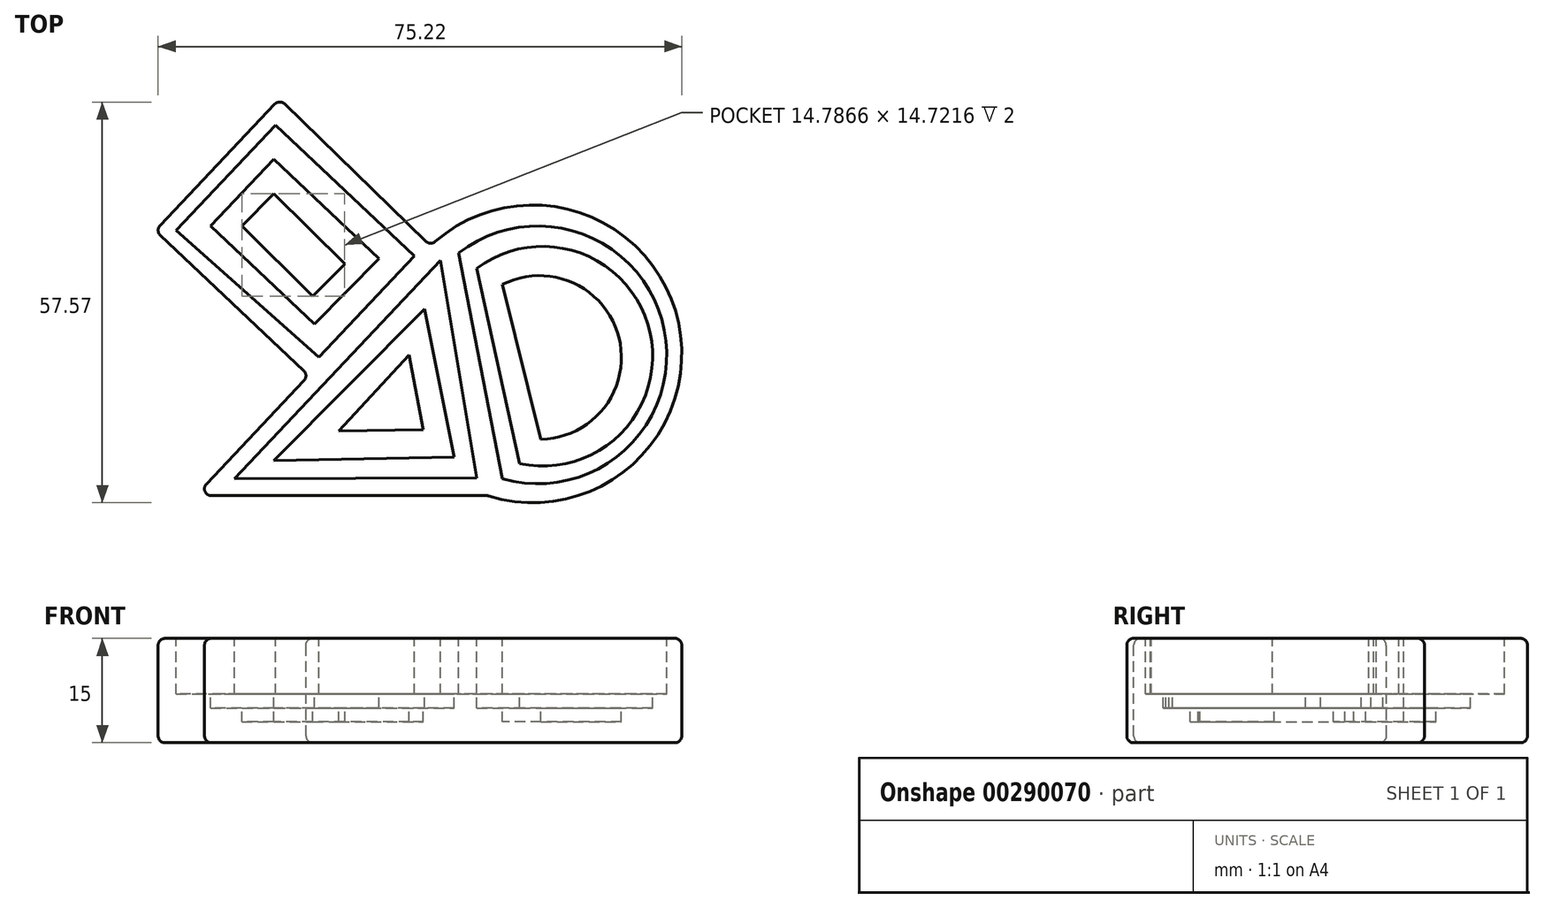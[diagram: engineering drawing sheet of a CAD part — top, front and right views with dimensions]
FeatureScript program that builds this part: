
annotation { "Feature Type Name" : "Feature", "Feature Type Description" : "" }
export const myFeature = defineFeature(function(context is Context, id is Id, definition is map)
    precondition{}
    {
        {
            var Q0;
            Q0=qCreatedBy(makeId("Top.planeOp"),FACE);
            var sketch = newSketch(context, id + "F0", { "sketchPlane" : qUnion([Q0])});
            skLineSegment(sketch, "E0", {"start": v(-46.18, 20.15) * mm, "end": v(-28.32, 39.05) * mm});
            skLineSegment(sketch, "E1", {"start": v(-28.32, 39.05) * mm, "end": v(-6.65, 17.95) * mm});
            skArc(sketch, "E2", {"start": v(1.58, -17.95) * mm, "mid": v(28.9, 7.21) * mm, "end": v(-6.65, 17.95) * mm});
            skLineSegment(sketch, "E3", {"start": v(-46.18, 20.15) * mm, "end": v(-24.13, -0.7) * mm});
            skLineSegment(sketch, "E4", {"start": v(-24.13, -0.7) * mm, "end": v(-40.43, -17.95) * mm});
            skLineSegment(sketch, "E5", {"start": v(-40.43, -17.95) * mm, "end": v(1.58, -17.95) * mm});
            skSolve(sketch);
        }
        {
            var Q0;
            Q0=makeQuery(id+"F0.imprint","IMPRINT",FACE,{"disambiguationData":[TD([[makeQuery(id+"F0.imprint","IMPRINT",EDGE,{"derivedFrom":sQuery(id+"F0.wireOp",EDGE,"E0")}),-1.0]])]});
            extrude(context, id + "F1", {"entities" : qUnion([Q0]), "depth" : 15 * mm});
        }
        {
            var Q0;
            Q0=makeQuery(id+"F1.opExtrude","CAP_FACE",FACE,{"disambiguationData":[OSD([sQuery(id+"F0.wireOp",EDGE,"E0"),sQuery(id+"F0.wireOp",EDGE,"E1"),sQuery(id+"F0.wireOp",EDGE,"E2"),sQuery(id+"F0.wireOp",EDGE,"E3"),sQuery(id+"F0.wireOp",EDGE,"45Map7S6-xY7Q-KK4a-DzPV-caNNbyCEZp7A"),sQuery(id+"F0.wireOp",EDGE,"oJqrQrKj-ZpfX-hNZr-h9x0-pQ9A5762xfXI"),sQuery(id+"F0.wireOp",EDGE,"E4"),sQuery(id+"F0.wireOp",EDGE,"E5")])],"isStart":false});
            var sketch = newSketch(context, id + "F2", { "sketchPlane" : qUnion([Q0])});
            skLineSegment(sketch, "E6", {"start": v(-34.83, -15.53) * mm, "end": v(-5.2, 15.83) * mm});
            skLineSegment(sketch, "E7", {"start": v(-5.2, 15.83) * mm, "end": v(0, -15.41) * mm});
            skLineSegment(sketch, "E8", {"start": v(0, -15.41) * mm, "end": v(-34.83, -15.53) * mm});
            skLineSegment(sketch, "E9", {"start": v(-43.18, 20.15) * mm, "end": v(-28.87, 35.28) * mm});
            skLineSegment(sketch, "E10", {"start": v(-28.87, 35.28) * mm, "end": v(-8.98, 16.5) * mm});
            skLineSegment(sketch, "E11", {"start": v(-8.98, 16.5) * mm, "end": v(-22.7, 1.97) * mm});
            skLineSegment(sketch, "E12", {"start": v(-22.7, 1.97) * mm, "end": v(-43.18, 20.15) * mm});
            skArc(sketch, "E13", {"start": v(3.7, -15.54) * mm, "mid": v(26.95, 5.82) * mm, "end": v(-2.6, 16.92) * mm});
            skPoint(sketch, "E13.endSnap0", {"position": v(-2.6, 0.2) * mm});
            skLineSegment(sketch, "E14", {"start": v(-2.6, 16.92) * mm, "end": v(3.7, -15.54) * mm});
            skSolve(sketch);
        }
        {
            var Q0;
            Q0=makeQuery(id+"F2.imprint","IMPRINT",FACE,{"disambiguationData":[TD([[makeQuery(id+"F2.imprint","IMPRINT",EDGE,{"derivedFrom":sQuery(id+"F2.wireOp",EDGE,"E13")}),1.0]])]});
            var Q1;
            Q1=makeQuery(id+"F2.imprint","IMPRINT",FACE,{"disambiguationData":[TD([[makeQuery(id+"F2.imprint","IMPRINT",EDGE,{"derivedFrom":sQuery(id+"F2.wireOp",EDGE,"E6")}),-1.0]])]});
            var Q2;
            Q2=makeQuery(id+"F2.imprint","IMPRINT",FACE,{"disambiguationData":[TD([[makeQuery(id+"F2.imprint","IMPRINT",EDGE,{"derivedFrom":sQuery(id+"F2.wireOp",EDGE,"E9")}),-1.0]])]});
            var Q3;
            Q3=makeQuery(id+"F2.imprint","IMPRINT",FACE,{"disambiguationData":[TD([[makeQuery(id+"F2.imprint","IMPRINT",EDGE,{"derivedFrom":sQuery(id+"F2.wireOp",EDGE,"E75luK8p-h0mA-NWcP-ZvuT-SGWaBSsSdRoQ")}),1.0]])]});
            extrude(context, id + "F3", {"entities" : qUnion([Q0, Q1, Q2, Q3]), "operationType" : NewBodyOperationType.REMOVE, "oppositeDirection" : true, "depth" : 8 * mm});
        }
        {
            var Q0;
            Q0=makeQuery(id+"F1.opExtrude","CAP_FACE",FACE,{"disambiguationData":[OSD([sQuery(id+"F0.wireOp",EDGE,"E0"),sQuery(id+"F0.wireOp",EDGE,"E1"),sQuery(id+"F0.wireOp",EDGE,"E2"),sQuery(id+"F0.wireOp",EDGE,"E3"),sQuery(id+"F0.wireOp",EDGE,"45Map7S6-xY7Q-KK4a-DzPV-caNNbyCEZp7A"),sQuery(id+"F0.wireOp",EDGE,"oJqrQrKj-ZpfX-hNZr-h9x0-pQ9A5762xfXI"),sQuery(id+"F0.wireOp",EDGE,"E4"),sQuery(id+"F0.wireOp",EDGE,"E5")])],"isStart":true});
            var Q1;
            Q1=makeQuery(id+"F3.boolean.opBoolean","COPY",EDGE,{"derivedFrom":makeQuery(id+"F3.opExtrude","CAP_EDGE",EDGE,{"disambiguationData":[OSD([sQuery(id+"F2.wireOp",EDGE,"E10")])],"isStart":true})});
            var Q2;
            Q2=makeQuery(id+"F3.boolean.opBoolean","COPY",EDGE,{"derivedFrom":makeQuery(id+"F3.opExtrude","CAP_EDGE",EDGE,{"disambiguationData":[OSD([sQuery(id+"F2.wireOp",EDGE,"E9")])],"isStart":true})});
            var Q3;
            Q3=makeQuery(id+"F3.boolean.opBoolean","COPY",EDGE,{"derivedFrom":makeQuery(id+"F3.opExtrude","CAP_EDGE",EDGE,{"disambiguationData":[OSD([sQuery(id+"F2.wireOp",EDGE,"E12")])],"isStart":true})});
            var Q4;
            Q4=makeQuery(id+"F3.boolean.opBoolean","COPY",EDGE,{"derivedFrom":makeQuery(id+"F3.opExtrude","CAP_EDGE",EDGE,{"disambiguationData":[OSD([sQuery(id+"F2.wireOp",EDGE,"E11")])],"isStart":true})});
            var Q5;
            Q5=makeQuery(id+"F3.boolean.opBoolean","COPY",EDGE,{"derivedFrom":makeQuery(id+"F3.opExtrude","CAP_EDGE",EDGE,{"disambiguationData":[OSD([sQuery(id+"F2.wireOp",EDGE,"E8")])],"isStart":true})});
            var Q6;
            Q6=makeQuery(id+"F3.boolean.opBoolean","COPY",EDGE,{"derivedFrom":makeQuery(id+"F3.opExtrude","CAP_EDGE",EDGE,{"disambiguationData":[OSD([sQuery(id+"F2.wireOp",EDGE,"E6")])],"isStart":true})});
            var Q7;
            Q7=makeQuery(id+"F3.boolean.opBoolean","COPY",EDGE,{"derivedFrom":makeQuery(id+"F3.opExtrude","CAP_EDGE",EDGE,{"disambiguationData":[OSD([sQuery(id+"F2.wireOp",EDGE,"E7")])],"isStart":true})});
            var Q8;
            Q8=makeQuery(id+"F3.boolean.opBoolean","COPY",EDGE,{"derivedFrom":makeQuery(id+"F3.opExtrude","CAP_EDGE",EDGE,{"disambiguationData":[OSD([sQuery(id+"F2.wireOp",EDGE,"E14")])],"isStart":true})});
            var Q9;
            Q9=makeQuery(id+"F3.boolean.opBoolean","COPY",EDGE,{"derivedFrom":makeQuery(id+"F3.opExtrude","CAP_EDGE",EDGE,{"disambiguationData":[OSD([sQuery(id+"F2.wireOp",EDGE,"E13")])],"isStart":true})});
            var Q10;
            Q10=makeQuery(id+"F3.boolean.opBoolean","COPY",EDGE,{"derivedFrom":makeQuery(id+"F3.opExtrude","CAP_EDGE",EDGE,{"disambiguationData":[OSD([sQuery(id+"F2.wireOp",EDGE,"RLaE2rvH-VrAM-fzAG-Qmya-pUEfVkDLwuKn")])],"isStart":true})});
            var Q11;
            Q11=makeQuery(id+"F3.boolean.opBoolean","COPY",EDGE,{"derivedFrom":makeQuery(id+"F3.opExtrude","CAP_EDGE",EDGE,{"disambiguationData":[OSD([sQuery(id+"F2.wireOp",EDGE,"jPx8ZiLx-Io0g-C835-jTOn-4QVJeUnpCxqh")])],"isStart":true})});
            var Q12;
            Q12=makeQuery(id+"F3.boolean.opBoolean","COPY",EDGE,{"derivedFrom":makeQuery(id+"F3.opExtrude","CAP_EDGE",EDGE,{"disambiguationData":[OSD([sQuery(id+"F2.wireOp",EDGE,"pincXrsu-reRM-YMyk-YWri-BdmM8ugr5dqy")])],"isStart":true})});
            var Q13;
            Q13=makeQuery(id+"F3.boolean.opBoolean","COPY",EDGE,{"derivedFrom":makeQuery(id+"F3.opExtrude","CAP_EDGE",EDGE,{"disambiguationData":[OSD([sQuery(id+"F2.wireOp",EDGE,"E75luK8p-h0mA-NWcP-ZvuT-SGWaBSsSdRoQ")])],"isStart":true})});
            var Q14;
            Q14=makeQuery(id+"F1.opExtrude","CAP_EDGE",EDGE,{"disambiguationData":[OSD([sQuery(id+"F0.wireOp",EDGE,"E2")])],"isStart":false});
            var Q15;
            Q15=makeQuery(id+"F1.opExtrude","CAP_EDGE",EDGE,{"disambiguationData":[OSD([sQuery(id+"F0.wireOp",EDGE,"oJqrQrKj-ZpfX-hNZr-h9x0-pQ9A5762xfXI")])],"isStart":false});
            var Q16;
            Q16=makeQuery(id+"F1.opExtrude","CAP_EDGE",EDGE,{"disambiguationData":[OSD([sQuery(id+"F0.wireOp",EDGE,"45Map7S6-xY7Q-KK4a-DzPV-caNNbyCEZp7A")])],"isStart":false});
            var Q17;
            Q17=makeQuery(id+"F1.opExtrude","CAP_EDGE",EDGE,{"disambiguationData":[OSD([sQuery(id+"F0.wireOp",EDGE,"E5")])],"isStart":false});
            var Q18;
            Q18=makeQuery(id+"F1.opExtrude","CAP_EDGE",EDGE,{"disambiguationData":[OSD([sQuery(id+"F0.wireOp",EDGE,"E4")])],"isStart":false});
            var Q19;
            Q19=makeQuery(id+"F1.opExtrude","CAP_EDGE",EDGE,{"disambiguationData":[OSD([sQuery(id+"F0.wireOp",EDGE,"E3")])],"isStart":false});
            var Q20;
            Q20=makeQuery(id+"F1.opExtrude","CAP_EDGE",EDGE,{"disambiguationData":[OSD([sQuery(id+"F0.wireOp",EDGE,"E0")])],"isStart":false});
            var Q21;
            Q21=makeQuery(id+"F1.opExtrude","CAP_EDGE",EDGE,{"disambiguationData":[OSD([sQuery(id+"F0.wireOp",EDGE,"E1")])],"isStart":false});
            var Q22;
            Q22=makeQuery(id+"F1.opExtrude","SWEPT_EDGE",EDGE,{"disambiguationData":[OSD([sQuery(id+"F0.wireOp",EDGE,"45Map7S6-xY7Q-KK4a-DzPV-caNNbyCEZp7A"),sQuery(id+"F0.wireOp",EDGE,"E5")])]});
            var Q23;
            Q23=makeQuery(id+"F1.opExtrude","SWEPT_FACE",FACE,{"disambiguationData":[OSD([sQuery(id+"F0.wireOp",EDGE,"oJqrQrKj-ZpfX-hNZr-h9x0-pQ9A5762xfXI")])]});
            var Q24;
            Q24=makeQuery(id+"F1.opExtrude","SWEPT_EDGE",EDGE,{"disambiguationData":[OSD([sQuery(id+"F0.wireOp",EDGE,"E1"),sQuery(id+"F0.wireOp",EDGE,"E2")])]});
            var Q25;
            Q25=makeQuery(id+"F1.opExtrude","SWEPT_FACE",FACE,{"disambiguationData":[OSD([sQuery(id+"F0.wireOp",EDGE,"E1")])]});
            var Q26;
            Q26=makeQuery(id+"F1.opExtrude","SWEPT_EDGE",EDGE,{"disambiguationData":[OSD([sQuery(id+"F0.wireOp",EDGE,"E0"),sQuery(id+"F0.wireOp",EDGE,"E1")])]});
            var Q27;
            Q27=makeQuery(id+"F1.opExtrude","SWEPT_EDGE",EDGE,{"disambiguationData":[OSD([sQuery(id+"F0.wireOp",EDGE,"E0"),sQuery(id+"F0.wireOp",EDGE,"E3")])]});
            var Q28;
            Q28=makeQuery(id+"F1.opExtrude","SWEPT_EDGE",EDGE,{"disambiguationData":[OSD([sQuery(id+"F0.wireOp",EDGE,"E4"),sQuery(id+"F0.wireOp",EDGE,"E5")])]});
            var Q29;
            Q29=makeQuery(id+"F1.opExtrude","SWEPT_EDGE",EDGE,{"disambiguationData":[OSD([sQuery(id+"F0.wireOp",EDGE,"E3"),sQuery(id+"F0.wireOp",EDGE,"E4")])]});
            var Q30;
            Q30=makeQuery(id+"F1.opExtrude","SWEPT_FACE",FACE,{"disambiguationData":[OSD([sQuery(id+"F0.wireOp",EDGE,"E5")])]});
            var Q31;
            Q31=makeQuery(id+"F1.opExtrude","SWEPT_EDGE",EDGE,{"disambiguationData":[OSD([sQuery(id+"F0.wireOp",EDGE,"E2"),sQuery(id+"F0.wireOp",EDGE,"oJqrQrKj-ZpfX-hNZr-h9x0-pQ9A5762xfXI")])]});
            fillet(context, id + "F4", {"entities" : qUnion([Q0, Q1, Q2, Q3, Q4, Q5, Q6, Q7, Q8, Q9, Q10, Q11, Q12, Q13, Q14, Q15, Q16, Q17, Q18, Q19, Q20, Q21, Q22, Q23, Q24, Q25, Q26, Q27, Q28, Q29, Q30, Q31]), "radius" : 1 * mm, "tangentPropagation" : true, "allowEdgeOverflow" : false});
        }
        {
            var Q0;
            Q0=makeQuery(id+"F3.boolean.opBoolean","COPY",FACE,{"derivedFrom":makeQuery(id+"F3.opExtrude","CAP_FACE",FACE,{"disambiguationData":[OSD([sQuery(id+"F2.wireOp",EDGE,"E9"),sQuery(id+"F2.wireOp",EDGE,"E10"),sQuery(id+"F2.wireOp",EDGE,"E11"),sQuery(id+"F2.wireOp",EDGE,"E12")])],"isStart":false})});
            var sketch = newSketch(context, id + "F5", { "sketchPlane" : qUnion([Q0])});
            skLineSegment(sketch, "E15", {"start": v(-3.25, -12.4) * mm, "end": v(-7.5, 8.88) * mm});
            skLineSegment(sketch, "E16", {"start": v(-7.5, 8.88) * mm, "end": v(-29.17, -12.9) * mm});
            skLineSegment(sketch, "E17", {"start": v(-29.17, -12.9) * mm, "end": v(-3.25, -12.4) * mm});
            skLineSegment(sketch, "E18", {"start": v(-14.05, 16.12) * mm, "end": v(-29.17, 30.4) * mm});
            skLineSegment(sketch, "E19", {"start": v(-29.17, 30.4) * mm, "end": v(-38.22, 20.83) * mm});
            skLineSegment(sketch, "E20", {"start": v(-38.22, 20.83) * mm, "end": v(-23.31, 6.74) * mm});
            skLineSegment(sketch, "E21", {"start": v(-23.31, 6.74) * mm, "end": v(-14.05, 16.12) * mm});
            skArc(sketch, "E22", {"start": v(6.18, -13.33) * mm, "mid": v(24.89, 5.49) * mm, "end": v(0, 14.7) * mm});
            skLineSegment(sketch, "E23", {"start": v(0, 14.7) * mm, "end": v(6.18, -13.33) * mm});
            skSolve(sketch);
        }
        {
            var Q0;
            Q0 = qSketchRegion(id + "F5", true);
            extrude(context, id + "F6", {"entities" : qUnion([Q0]), "operationType" : NewBodyOperationType.REMOVE, "oppositeDirection" : true, "depth" : 2 * mm});
        }
        {
            var Q0;
            Q0=makeQuery(id+"F6.boolean.opBoolean","COPY",FACE,{"derivedFrom":makeQuery(id+"F6.opExtrude","CAP_FACE",FACE,{"disambiguationData":[OSD([sQuery(id+"F5.wireOp",EDGE,"E22"),sQuery(id+"F5.wireOp",EDGE,"E23")])],"isStart":false})});
            var sketch = newSketch(context, id + "F7", { "sketchPlane" : qUnion([Q0])});
            skArc(sketch, "E24", {"start": v(9.23, -9.85) * mm, "mid": v(20.42, 4.75) * mm, "end": v(3.7, 12.4) * mm});
            skLineSegment(sketch, "E25", {"start": v(9.23, -9.85) * mm, "end": v(3.7, 12.4) * mm});
            skSolve(sketch);
        }
        {
            var Q0;
            Q0=makeQuery(id+"F7.imprint","IMPRINT",FACE,{"disambiguationData":[TD([[makeQuery(id+"F7.imprint","IMPRINT",EDGE,{"derivedFrom":sQuery(id+"F7.wireOp",EDGE,"E24")}),1.0]])]});
            extrude(context, id + "F8", {"entities" : qUnion([Q0]), "operationType" : NewBodyOperationType.REMOVE, "oppositeDirection" : true, "depth" : 2 * mm});
        }
        {
            var Q0;
            Q0=makeQuery(id+"F6.boolean.opBoolean","COPY",FACE,{"derivedFrom":makeQuery(id+"F6.opExtrude","CAP_FACE",FACE,{"disambiguationData":[OSD([sQuery(id+"F5.wireOp",EDGE,"E15"),sQuery(id+"F5.wireOp",EDGE,"E16"),sQuery(id+"F5.wireOp",EDGE,"E17")])],"isStart":false})});
            var sketch = newSketch(context, id + "F9", { "sketchPlane" : qUnion([Q0])});
            skLineSegment(sketch, "E26", {"start": v(-19.81, -8.67) * mm, "end": v(-7.67, -8.44) * mm});
            skLineSegment(sketch, "E27", {"start": v(-7.67, -8.44) * mm, "end": v(-9.7, 2.24) * mm});
            skLineSegment(sketch, "E28", {"start": v(-9.7, 2.24) * mm, "end": v(-19.81, -8.67) * mm});
            skSolve(sketch);
        }
        {
            var Q0;
            Q0=makeQuery(id+"F9.imprint","IMPRINT",FACE,{"disambiguationData":[TD([[makeQuery(id+"F9.imprint","IMPRINT",EDGE,{"derivedFrom":sQuery(id+"F9.wireOp",EDGE,"E26")}),1.0]])]});
            extrude(context, id + "F10", {"entities" : qUnion([Q0]), "operationType" : NewBodyOperationType.REMOVE, "oppositeDirection" : true, "depth" : 2 * mm});
        }
        {
            var Q0;
            Q0=makeQuery(id+"F6.boolean.opBoolean","COPY",FACE,{"derivedFrom":makeQuery(id+"F6.opExtrude","CAP_FACE",FACE,{"disambiguationData":[OSD([sQuery(id+"F5.wireOp",EDGE,"E18"),sQuery(id+"F5.wireOp",EDGE,"E19"),sQuery(id+"F5.wireOp",EDGE,"E20"),sQuery(id+"F5.wireOp",EDGE,"E21")])],"isStart":false})});
            var sketch = newSketch(context, id + "F11", { "sketchPlane" : qUnion([Q0])});
            skLineSegment(sketch, "E29", {"start": v(-23.58, 10.7) * mm, "end": v(-18.96, 15.37) * mm});
            skLineSegment(sketch, "E30", {"start": v(-18.96, 15.37) * mm, "end": v(-29.17, 25.46) * mm});
            skLineSegment(sketch, "E31", {"start": v(-29.17, 25.46) * mm, "end": v(-33.75, 20.83) * mm});
            skLineSegment(sketch, "E32", {"start": v(-33.75, 20.83) * mm, "end": v(-23.54, 10.74) * mm});
            skSolve(sketch);
        }
        {
            var Q0;
            {var subQ0=sQuery(id+"F11.wireOp",EDGE,"E30");Q0=makeQuery(id+"F11.imprint","IMPRINT",FACE,{"disambiguationData":[TD([[makeQuery(id+"F11.imprint","IMPRINT",EDGE,{"derivedFrom":subQ0}),1.0]])]});}
            extrude(context, id + "F12", {"entities" : qUnion([Q0]), "operationType" : NewBodyOperationType.REMOVE, "oppositeDirection" : true, "depth" : 2 * mm});
        }
    });
